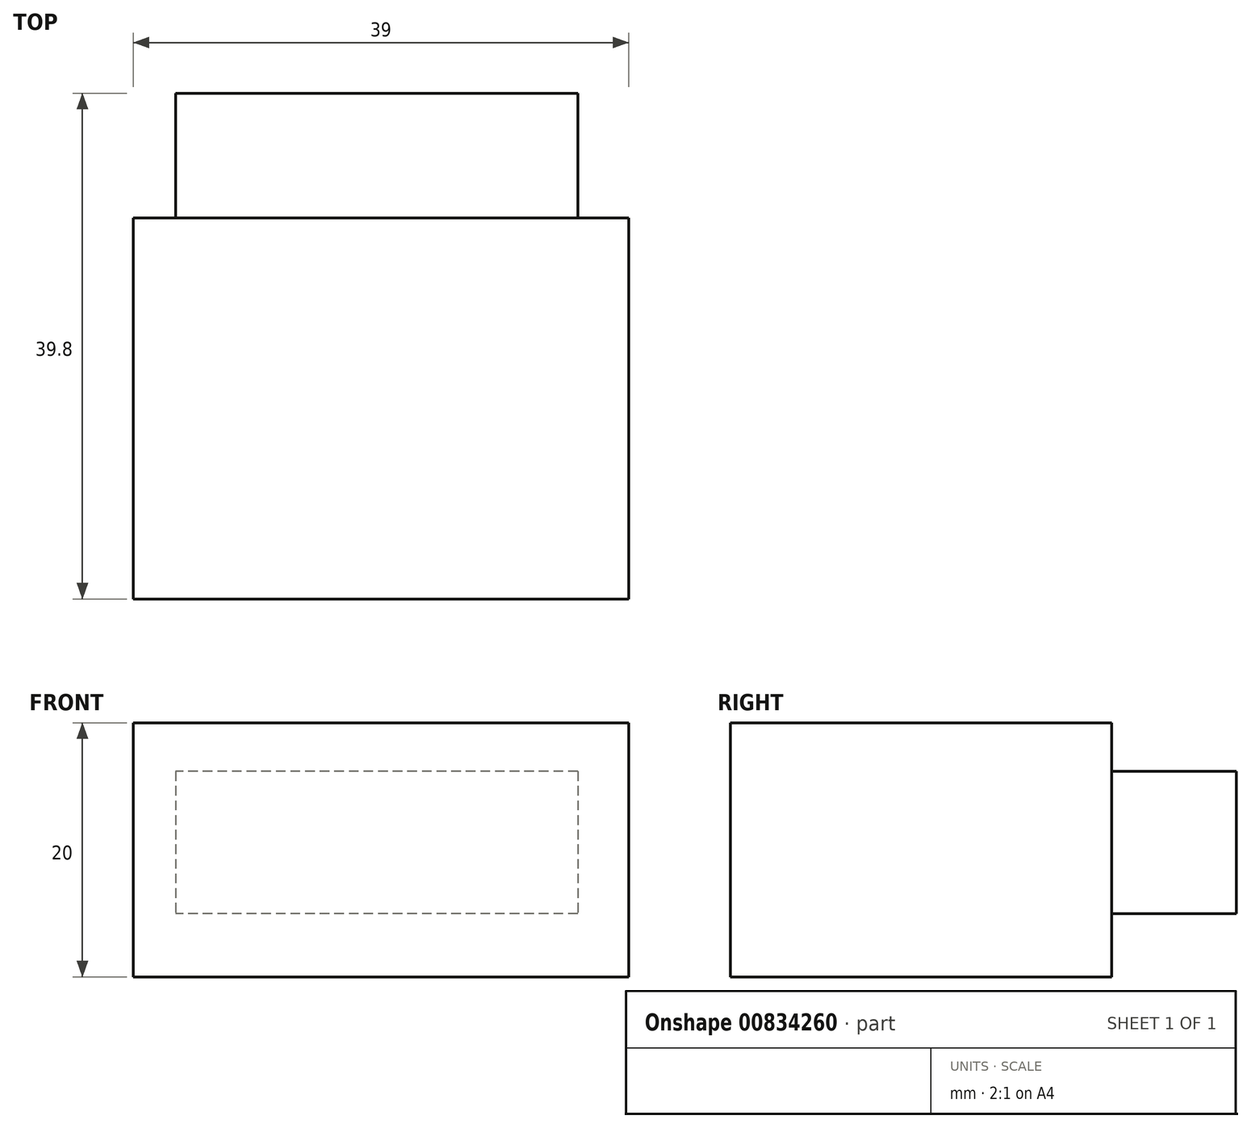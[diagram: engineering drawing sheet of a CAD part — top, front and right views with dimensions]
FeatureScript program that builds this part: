
annotation { "Feature Type Name" : "Feature", "Feature Type Description" : "" }
export const myFeature = defineFeature(function(context is Context, id is Id, definition is map)
    precondition{}
    {
        {
            var Q0;
            Q0=qCreatedBy(makeId("Front.planeOp"),FACE);
            var sketch = newSketch(context, id + "F0", { "sketchPlane" : qUnion([Q0])});
            skLineSegment(sketch, "E0.bottom", {"start": v(-19.5, 10) * mm, "end": v(19.5, 10) * mm});
            skLineSegment(sketch, "E0.top", {"start": v(-19.5, -10) * mm, "end": v(19.5, -10) * mm});
            skLineSegment(sketch, "E0.left", {"start": v(-19.5, 10) * mm, "end": v(-19.5, -10) * mm});
            skLineSegment(sketch, "E0.right", {"start": v(19.5, 10) * mm, "end": v(19.5, -10) * mm});
            skPoint(sketch, "E0.middle", {"position": v(0, 0) * mm});
            skSolve(sketch);
        }
        {
            var Q0;
            Q0=makeQuery(id+"F0.imprint","IMPRINT",FACE,{"disambiguationData":[TD([[makeQuery(id+"F0.imprint","IMPRINT",EDGE,{"derivedFrom":sQuery(id+"F0.wireOp",EDGE,"E0.bottom")}),-1.0]])]});
            extrude(context, id + "F1", {"entities" : qUnion([Q0]), "depth" : 30 * mm, "offsetDistance" : 25 * mm});
        }
        {
            var Q0;
            Q0=makeQuery(id+"F1.opExtrude","CAP_FACE",FACE,{"disambiguationData":[OSD([sQuery(id+"F0.wireOp",EDGE,"E0.bottom"),sQuery(id+"F0.wireOp",EDGE,"E0.top"),sQuery(id+"F0.wireOp",EDGE,"E0.left"),sQuery(id+"F0.wireOp",EDGE,"E0.right")])],"isStart":false});
            var sketch = newSketch(context, id + "F2", { "sketchPlane" : qUnion([Q0])});
            skLineSegment(sketch, "E1.bottom", {"start": v(15.47, 6.17) * mm, "end": v(-16.15, 6.17) * mm});
            skLineSegment(sketch, "E1.top", {"start": v(15.47, -5.02) * mm, "end": v(-16.15, -5.02) * mm});
            skLineSegment(sketch, "E1.left", {"start": v(15.47, 6.17) * mm, "end": v(15.47, -5.02) * mm});
            skLineSegment(sketch, "E1.right", {"start": v(-16.15, 6.17) * mm, "end": v(-16.15, -5.02) * mm});
            skSolve(sketch);
        }
        {
            var Q0;
            Q0=makeQuery(id+"F2.imprint","IMPRINT",FACE,{"disambiguationData":[TD([[makeQuery(id+"F2.imprint","IMPRINT",EDGE,{"derivedFrom":sQuery(id+"F2.wireOp",EDGE,"E1.bottom")}),1.0]])]});
            extrude(context, id + "F3", {"entities" : qUnion([Q0]), "operationType" : NewBodyOperationType.ADD, "oppositeDirection" : true, "depth" : 39.8 * mm, "offsetDistance" : 25 * mm});
        }
    });
